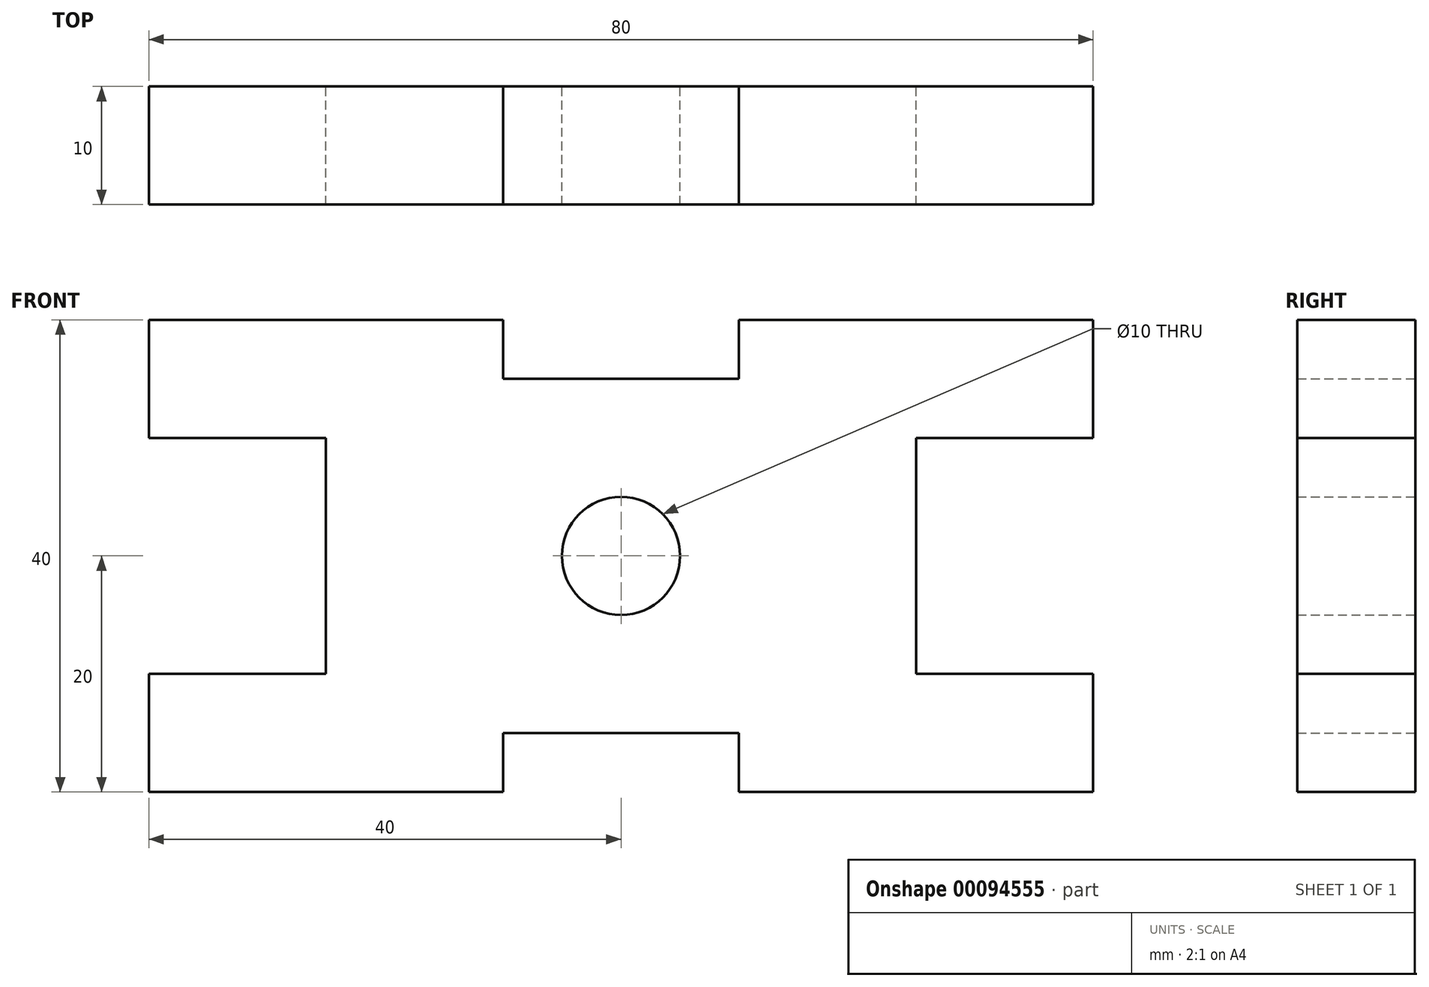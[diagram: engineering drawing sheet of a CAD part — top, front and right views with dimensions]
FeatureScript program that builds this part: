
annotation { "Feature Type Name" : "Feature", "Feature Type Description" : "" }
export const myFeature = defineFeature(function(context is Context, id is Id, definition is map)
    precondition{}
    {
        {
            var Q0;
            Q0=qCreatedBy(makeId("Front.planeOp"),FACE);
            var sketch = newSketch(context, id + "F0", { "sketchPlane" : qUnion([Q0])});
            skLineSegment(sketch, "E0", {"start": v(0, 0) * mm, "end": v(30, 0) * mm});
            skLineSegment(sketch, "E1", {"start": v(80, 0) * mm, "end": v(80, 10) * mm});
            skLineSegment(sketch, "E2", {"start": v(80, 40) * mm, "end": v(50, 40) * mm});
            skLineSegment(sketch, "E3", {"start": v(0, 40) * mm, "end": v(0, 30) * mm});
            skLineSegment(sketch, "E4", {"start": v(30, 5) * mm, "end": v(50, 5) * mm});
            skLineSegment(sketch, "E5", {"start": v(50, 5) * mm, "end": v(50, 0) * mm});
            skLineSegment(sketch, "E6", {"start": v(30, 5) * mm, "end": v(30, 0) * mm});
            skLineSegment(sketch, "E7.trimOffspring", {"start": v(50, 0) * mm, "end": v(80, 0) * mm});
            skLineSegment(sketch, "E8", {"start": v(15, 30) * mm, "end": v(15, 10) * mm});
            skLineSegment(sketch, "E9", {"start": v(15, 10) * mm, "end": v(0, 10) * mm});
            skLineSegment(sketch, "E10", {"start": v(15, 30) * mm, "end": v(0, 30) * mm});
            skLineSegment(sketch, "E11", {"start": v(65, 30) * mm, "end": v(65, 10) * mm});
            skLineSegment(sketch, "E12", {"start": v(65, 10) * mm, "end": v(80, 10) * mm});
            skLineSegment(sketch, "E13", {"start": v(65, 30) * mm, "end": v(80, 30) * mm});
            skLineSegment(sketch, "E14", {"start": v(30, 35) * mm, "end": v(50, 35) * mm});
            skLineSegment(sketch, "E15", {"start": v(50, 35) * mm, "end": v(50, 40) * mm});
            skLineSegment(sketch, "E16", {"start": v(30, 35) * mm, "end": v(30, 40) * mm});
            skLineSegment(sketch, "E17.trimOffspring", {"start": v(0, 10) * mm, "end": v(0, 0) * mm});
            skLineSegment(sketch, "E18.trimOffspring", {"start": v(30, 40) * mm, "end": v(0, 40) * mm});
            skLineSegment(sketch, "E19.trimOffspring", {"start": v(80, 30) * mm, "end": v(80, 40) * mm});
            skCircle(sketch, "E20", {"center": v(40, 20) * mm, "radius": 5 * mm});
            skPoint(sketch, "E20.centerSnap0", {"position": v(40, 35) * mm});
            skSolve(sketch);
        }
        {
            var Q0;
            Q0=makeQuery(id+"F0.imprint","IMPRINT",FACE,{"disambiguationData":[TD([[makeQuery(id+"F0.imprint","IMPRINT",EDGE,{"derivedFrom":sQuery(id+"F0.wireOp",EDGE,"E0")}),1.0]])]});
            extrude(context, id + "F1", {"entities" : qUnion([Q0]), "depth" : 10 * mm});
        }
    });
